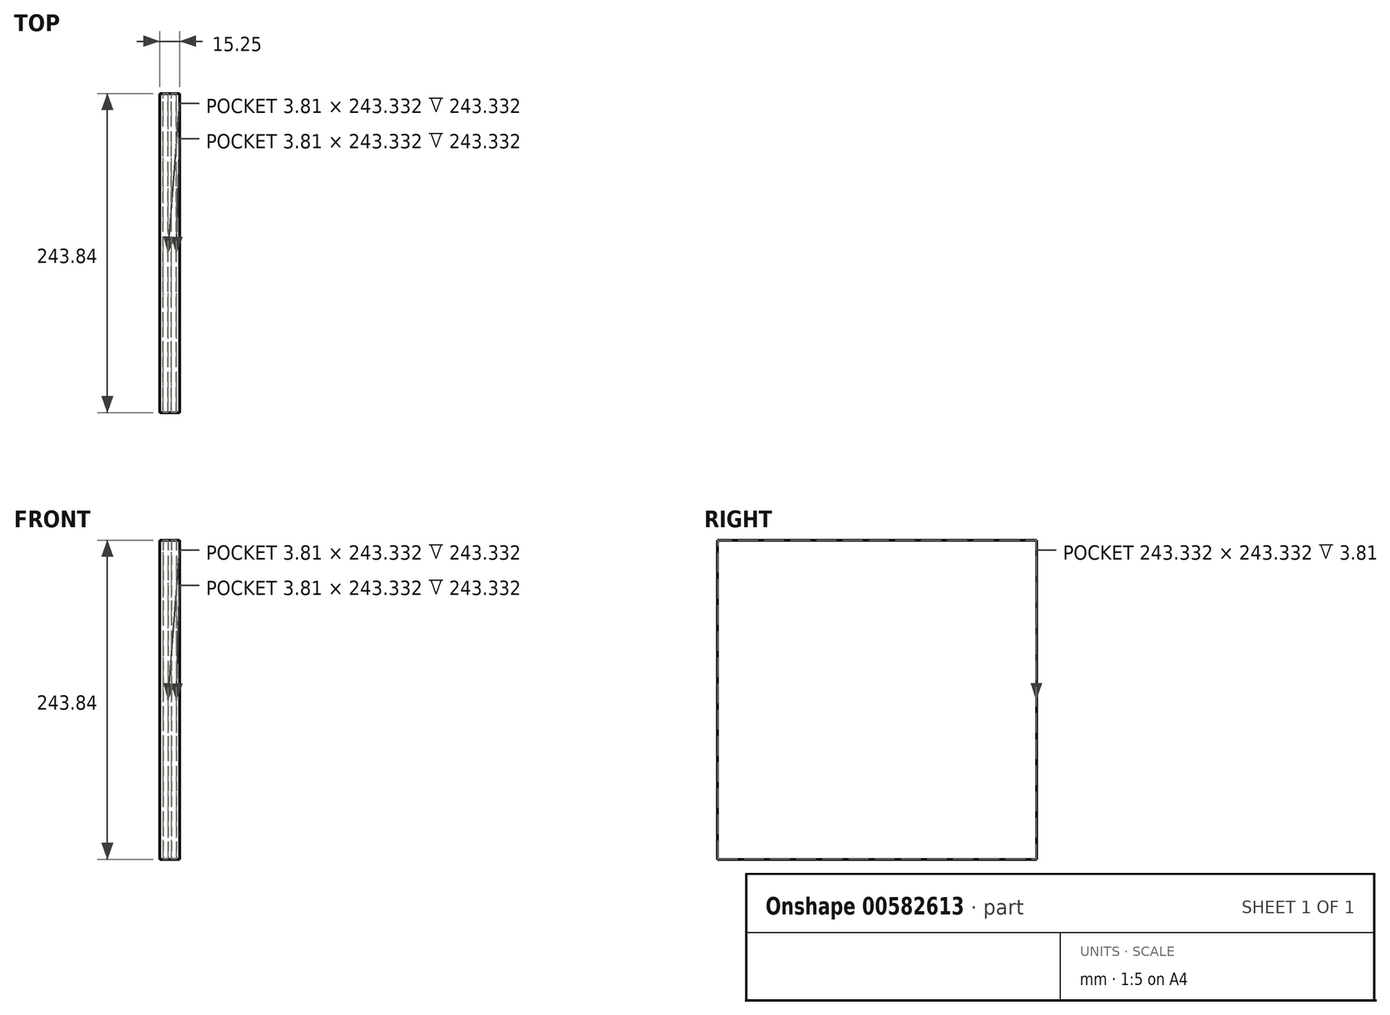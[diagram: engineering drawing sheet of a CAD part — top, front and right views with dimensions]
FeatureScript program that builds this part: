
annotation { "Feature Type Name" : "Feature", "Feature Type Description" : "" }
export const myFeature = defineFeature(function(context is Context, id is Id, definition is map)
    precondition{}
    {
        {
            var Q0;
            Q0=qCreatedBy(makeId("Front.planeOp"),FACE);
            var sketch = newSketch(context, id + "F0", { "sketchPlane" : qUnion([Q0])});
            skLineSegment(sketch, "E0.bottom", {"start": v(0, 0) * mm, "end": v(15.24, 0) * mm});
            skLineSegment(sketch, "E0.top", {"start": v(0, -243.84) * mm, "end": v(15.24, -243.84) * mm});
            skLineSegment(sketch, "E0.left", {"start": v(0, 0) * mm, "end": v(0, -243.84) * mm});
            skLineSegment(sketch, "E0.right", {"start": v(15.24, 0) * mm, "end": v(15.24, -243.84) * mm});
            skSolve(sketch);
        }
        {
            var Q0;
            Q0=makeQuery(id+"F0.imprint","IMPRINT",FACE,{"disambiguationData":[TD([[makeQuery(id+"F0.imprint","IMPRINT",EDGE,{"derivedFrom":sQuery(id+"F0.wireOp",EDGE,"E0.bottom")}),-1.0]])]});
            extrude(context, id + "F1", {"entities" : qUnion([Q0]), "depth" : 0.25 * mm, "offsetDistance" : 25.4 * mm});
        }
        {
            var Q0;
            Q0=makeQuery(id+"F1.opExtrude","CAP_FACE",FACE,{"disambiguationData":[OSD([sQuery(id+"F0.wireOp",EDGE,"E0.bottom"),sQuery(id+"F0.wireOp",EDGE,"E0.top"),sQuery(id+"F0.wireOp",EDGE,"E0.left"),sQuery(id+"F0.wireOp",EDGE,"E0.right")])],"isStart":false});
            var sketch = newSketch(context, id + "F2", { "sketchPlane" : qUnion([Q0])});
            skLineSegment(sketch, "E1.bottom", {"start": v(0, 0) * mm, "end": v(15.24, 0) * mm});
            skLineSegment(sketch, "E1.top", {"start": v(0, -0.25) * mm, "end": v(15.24, -0.25) * mm});
            skLineSegment(sketch, "E1.left", {"start": v(0, 0) * mm, "end": v(0, -0.25) * mm});
            skLineSegment(sketch, "E1.right", {"start": v(15.24, 0) * mm, "end": v(15.24, -0.25) * mm});
            skLineSegment(sketch, "E2.bottom", {"start": v(0, -243.84) * mm, "end": v(15.24, -243.84) * mm});
            skLineSegment(sketch, "E2.top", {"start": v(0, -243.59) * mm, "end": v(15.24, -243.59) * mm});
            skLineSegment(sketch, "E2.left", {"start": v(0, -243.84) * mm, "end": v(0, -243.59) * mm});
            skLineSegment(sketch, "E2.right", {"start": v(15.24, -243.84) * mm, "end": v(15.24, -243.59) * mm});
            skSolve(sketch);
        }
        {
            var Q0;
            Q0 = qSketchRegion(id + "F2", true);
            extrude(context, id + "F3", {"entities" : qUnion([Q0]), "operationType" : NewBodyOperationType.ADD, "depth" : 243.33 * mm, "offsetDistance" : 25.4 * mm});
        }
        {
            var Q0;
            Q0=makeQuery(id+"F3.opExtrude","CAP_FACE",FACE,{"disambiguationData":[OSD([sQuery(id+"F2.wireOp",EDGE,"E1.bottom"),sQuery(id+"F2.wireOp",EDGE,"E1.top"),sQuery(id+"F2.wireOp",EDGE,"E1.left"),sQuery(id+"F2.wireOp",EDGE,"E1.right")])],"isStart":false});
            var sketch = newSketch(context, id + "F4", { "sketchPlane" : qUnion([Q0])});
            skLineSegment(sketch, "E3.bottom", {"start": v(0, 0) * mm, "end": v(15.25, 0) * mm});
            skLineSegment(sketch, "E3.top", {"start": v(0, -243.84) * mm, "end": v(15.25, -243.84) * mm});
            skLineSegment(sketch, "E3.left", {"start": v(0, 0) * mm, "end": v(0, -243.84) * mm});
            skLineSegment(sketch, "E3.right", {"start": v(15.25, 0) * mm, "end": v(15.25, -243.84) * mm});
            skSolve(sketch);
        }
        {
            var Q0;
            Q0 = qSketchRegion(id + "F4", true);
            extrude(context, id + "F5", {"entities" : qUnion([Q0]), "operationType" : NewBodyOperationType.ADD, "depth" : 0.25 * mm, "offsetDistance" : 25.4 * mm});
        }
        {
            var Q0;
            Q0=makeQuery(id+"F3.opExtrude","SWEPT_FACE",FACE,{"disambiguationData":[OSD([sQuery(id+"F2.wireOp",EDGE,"E2.top")])]});
            var sketch = newSketch(context, id + "F6", { "sketchPlane" : qUnion([Q0])});
            skLineSegment(sketch, "E4.bottom", {"start": v(15.24, -243.59) * mm, "end": v(12.7, -243.59) * mm});
            skLineSegment(sketch, "E4.top", {"start": v(15.24, -0.25) * mm, "end": v(12.7, -0.25) * mm});
            skLineSegment(sketch, "E4.left", {"start": v(15.24, -243.59) * mm, "end": v(15.24, -0.25) * mm});
            skLineSegment(sketch, "E4.right", {"start": v(12.7, -243.59) * mm, "end": v(12.7, -0.25) * mm});
            skLineSegment(sketch, "E5.bottom", {"start": v(6.35, -243.59) * mm, "end": v(8.9, -243.59) * mm});
            skLineSegment(sketch, "E5.top", {"start": v(6.35, -0.25) * mm, "end": v(8.89, -0.25) * mm});
            skLineSegment(sketch, "E5.left", {"start": v(6.35, -243.59) * mm, "end": v(6.35, -0.25) * mm});
            skLineSegment(sketch, "E5.right", {"start": v(8.9, -243.59) * mm, "end": v(8.89, -0.25) * mm});
            skLineSegment(sketch, "E6.bottom", {"start": v(0, -243.59) * mm, "end": v(2.54, -243.59) * mm});
            skLineSegment(sketch, "E6.top", {"start": v(0, -0.25) * mm, "end": v(2.54, -0.25) * mm});
            skLineSegment(sketch, "E6.left", {"start": v(0, -243.59) * mm, "end": v(0, -0.25) * mm});
            skLineSegment(sketch, "E6.right", {"start": v(2.54, -243.59) * mm, "end": v(2.54, -0.25) * mm});
            skSolve(sketch);
        }
        {
            var Q0;
            Q0 = qSketchRegion(id + "F6", true);
            extrude(context, id + "F7", {"entities" : qUnion([Q0]), "operationType" : NewBodyOperationType.ADD, "depth" : 243.33 * mm, "offsetDistance" : 25.4 * mm});
        }
    });
